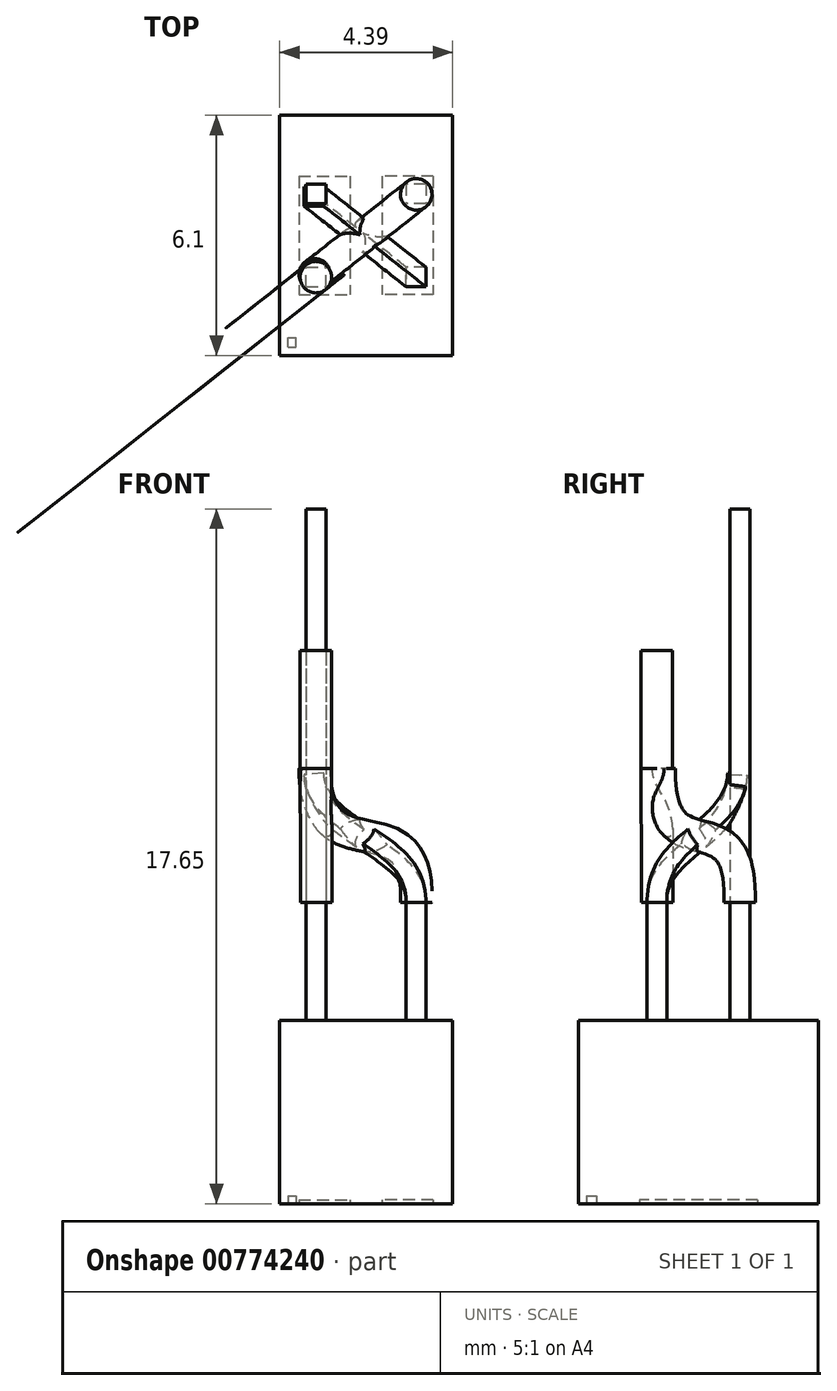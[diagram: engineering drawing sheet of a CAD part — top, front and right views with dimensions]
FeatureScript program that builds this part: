
annotation { "Feature Type Name" : "Feature", "Feature Type Description" : "" }
export const myFeature = defineFeature(function(context is Context, id is Id, definition is map)
    precondition{}
    {
        {
            var Q0;
            Q0=qCreatedBy(makeId("Top.planeOp"),FACE);
            var sketch = newSketch(context, id + "F0", { "sketchPlane" : qUnion([Q0])});
            skLineSegment(sketch, "E0.bottom", {"start": v(-4.39, 6.1) * mm, "end": v(0, 6.1) * mm});
            skLineSegment(sketch, "E0.top", {"start": v(-4.39, 0) * mm, "end": v(0, 0) * mm});
            skLineSegment(sketch, "E0.left", {"start": v(-4.39, 6.1) * mm, "end": v(-4.39, 0) * mm});
            skLineSegment(sketch, "E0.right", {"start": v(0, 6.1) * mm, "end": v(0, 0) * mm});
            skLineSegment(sketch, "E1", {"start": v(-2.2, -2.66) * mm, "end": v(-2.2, -2.66) * mm});
            skPoint(sketch, "E1.startSnap0", {"position": v(-2.2, 6.1) * mm});
            skPoint(sketch, "E1.endSnap0", {"position": v(-2.2, 0) * mm});
            skLineSegment(sketch, "E2", {"start": v(-4.39, 3.05) * mm, "end": v(0, 3.05) * mm, "construction": true});
            skLineSegment(sketch, "E3.bottom", {"start": v(-3.9, 4.55) * mm, "end": v(-2.6, 4.55) * mm});
            skLineSegment(sketch, "E3.top", {"start": v(-3.9, 1.55) * mm, "end": v(-2.6, 1.55) * mm});
            skLineSegment(sketch, "E3.left", {"start": v(-3.9, 4.55) * mm, "end": v(-3.9, 1.55) * mm});
            skLineSegment(sketch, "E3.right", {"start": v(-2.6, 4.55) * mm, "end": v(-2.6, 1.55) * mm});
            skLineSegment(sketch, "E4", {"start": v(-3.9, 3.05) * mm, "end": v(-2.6, 3.05) * mm, "construction": true});
            skLineSegment(sketch, "E5", {"start": v(-3.25, 4.55) * mm, "end": v(-3.25, 1.55) * mm, "construction": true});
            skLineSegment(sketch, "E6", {"start": v(-2.2, 6.61) * mm, "end": v(-2.2, -0.8) * mm, "construction": true});
            skLineSegment(sketch, "E7.MirrorCS", {"start": v(-1.79, 4.55) * mm, "end": v(-1.79, 1.55) * mm});
            skLineSegment(sketch, "E8.MirrorCS", {"start": v(-0.49, 4.55) * mm, "end": v(-1.79, 4.55) * mm});
            skLineSegment(sketch, "E9.MirrorCS", {"start": v(-0.49, 4.55) * mm, "end": v(-0.49, 1.55) * mm});
            skLineSegment(sketch, "E10.MirrorCS", {"start": v(-0.49, 1.55) * mm, "end": v(-1.79, 1.55) * mm});
            skLineSegment(sketch, "E11.bottom", {"start": v(-4.17, 0.2) * mm, "end": v(-3.97, 0.2) * mm});
            skLineSegment(sketch, "E11.top", {"start": v(-4.17, 0.46) * mm, "end": v(-3.97, 0.46) * mm});
            skLineSegment(sketch, "E11.left", {"start": v(-4.17, 0.2) * mm, "end": v(-4.17, 0.46) * mm});
            skLineSegment(sketch, "E11.right", {"start": v(-3.97, 0.2) * mm, "end": v(-3.97, 0.46) * mm});
            skSolve(sketch);
        }
        {
            var Q0;
            Q0=makeQuery(id+"F0.imprint","IMPRINT",FACE,{"disambiguationData":[TD([[makeQuery(id+"F0.imprint","IMPRINT",EDGE,{"derivedFrom":sQuery(id+"F0.wireOp",EDGE,"E0.bottom")}),-1.0]])]});
            var Q1;
            Q1=makeQuery(id+"F0.imprint","IMPRINT",FACE,{"disambiguationData":[TD([[makeQuery(id+"F0.imprint","IMPRINT",EDGE,{"derivedFrom":sQuery(id+"F0.wireOp",EDGE,"E3.bottom")}),-1.0]])]});
            var Q2;
            Q2=makeQuery(id+"F0.imprint","IMPRINT",FACE,{"disambiguationData":[TD([[makeQuery(id+"F0.imprint","IMPRINT",EDGE,{"derivedFrom":sQuery(id+"F0.wireOp",EDGE,"E7.MirrorCS")}),1.0]])]});
            var Q3;
            Q3=makeQuery(id+"F0.imprint","IMPRINT",FACE,{"disambiguationData":[TD([[makeQuery(id+"F0.imprint","IMPRINT",EDGE,{"derivedFrom":sQuery(id+"F0.wireOp",EDGE,"E11.bottom")}),1.0]])]});
            extrude(context, id + "F1", {"entities" : qUnion([Q0, Q1, Q2, Q3]), "depth" : 4.65 * mm, "offsetDistance" : 25 * mm});
        }
        {
            var Q0;
            Q0=makeQuery(id+"F0.imprint","IMPRINT",FACE,{"disambiguationData":[TD([[makeQuery(id+"F0.imprint","IMPRINT",EDGE,{"derivedFrom":sQuery(id+"F0.wireOp",EDGE,"E3.bottom")}),-1.0]])]});
            var Q1;
            Q1=makeQuery(id+"F0.imprint","IMPRINT",FACE,{"disambiguationData":[TD([[makeQuery(id+"F0.imprint","IMPRINT",EDGE,{"derivedFrom":sQuery(id+"F0.wireOp",EDGE,"E7.MirrorCS")}),1.0]])]});
            extrude(context, id + "F2", {"entities" : qUnion([Q0, Q1]), "operationType" : NewBodyOperationType.REMOVE, "depth" : .1 * mm, "offsetDistance" : 25 * mm});
        }
        {
            var Q0;
            Q0=makeQuery(id+"F1.opExtrude","CAP_FACE",FACE,{"disambiguationData":[OSD([sQuery(id+"F0.wireOp",EDGE,"E0.bottom"),sQuery(id+"F0.wireOp",EDGE,"E0.top"),sQuery(id+"F0.wireOp",EDGE,"E0.left"),sQuery(id+"F0.wireOp",EDGE,"E0.right")])],"isStart":false});
            var sketch = newSketch(context, id + "F3", { "sketchPlane" : qUnion([Q0])});
            skLineSegment(sketch, "E12", {"start": v(-2.2, 6.1) * mm, "end": v(-2.2, 0) * mm, "construction": true});
            skLineSegment(sketch, "E13", {"start": v(-4.39, 3.05) * mm, "end": v(0, 3.05) * mm, "construction": true});
            skLineSegment(sketch, "E14.bottom", {"start": v(-3.71, 4.35) * mm, "end": v(-3.21, 4.35) * mm});
            skLineSegment(sketch, "E14.top", {"start": v(-3.71, 3.85) * mm, "end": v(-3.21, 3.85) * mm});
            skLineSegment(sketch, "E14.left", {"start": v(-3.71, 4.35) * mm, "end": v(-3.71, 3.85) * mm});
            skLineSegment(sketch, "E14.right", {"start": v(-3.21, 4.35) * mm, "end": v(-3.21, 3.85) * mm});
            skLineSegment(sketch, "E15.MirrorCS", {"start": v(-1.17, 4.35) * mm, "end": v(-1.17, 3.85) * mm});
            skLineSegment(sketch, "E16.MirrorCS", {"start": v(-0.67, 4.35) * mm, "end": v(-1.17, 4.35) * mm});
            skLineSegment(sketch, "E17.MirrorCS", {"start": v(-0.68, 4.35) * mm, "end": v(-0.68, 3.85) * mm});
            skLineSegment(sketch, "E18.MirrorCS", {"start": v(-0.67, 3.85) * mm, "end": v(-1.17, 3.85) * mm});
            skLineSegment(sketch, "E19.MirrorCS", {"start": v(-3.71, 2.24) * mm, "end": v(-3.21, 2.24) * mm});
            skLineSegment(sketch, "E20.MirrorCS", {"start": v(-3.71, 1.75) * mm, "end": v(-3.71, 2.24) * mm});
            skLineSegment(sketch, "E21.MirrorCS", {"start": v(-3.71, 1.74) * mm, "end": v(-3.21, 1.74) * mm});
            skLineSegment(sketch, "E22.MirrorCS", {"start": v(-3.21, 1.75) * mm, "end": v(-3.21, 2.24) * mm});
            skLineSegment(sketch, "E23.MirrorCS", {"start": v(-1.17, 1.75) * mm, "end": v(-1.17, 2.24) * mm});
            skLineSegment(sketch, "E24.MirrorCS", {"start": v(-0.67, 1.74) * mm, "end": v(-1.17, 1.74) * mm});
            skLineSegment(sketch, "E25.MirrorCS", {"start": v(-0.68, 1.75) * mm, "end": v(-0.68, 2.24) * mm});
            skLineSegment(sketch, "E26.MirrorCS", {"start": v(-0.67, 2.24) * mm, "end": v(-1.17, 2.24) * mm});
            skSolve(sketch);
        }
        {
            var Q0;
            Q0=makeQuery(id+"F3.imprint","IMPRINT",FACE,{"disambiguationData":[TD([[makeQuery(id+"F3.imprint","IMPRINT",EDGE,{"derivedFrom":sQuery(id+"F3.wireOp",EDGE,"E14.bottom")}),-1.0]])]});
            var Q1;
            Q1=makeQuery(id+"F3.imprint","IMPRINT",FACE,{"disambiguationData":[TD([[makeQuery(id+"F3.imprint","IMPRINT",EDGE,{"derivedFrom":sQuery(id+"F3.wireOp",EDGE,"E19.MirrorCS")}),-1.0]])]});
            var Q2;
            Q2=makeQuery(id+"F3.imprint","IMPRINT",FACE,{"disambiguationData":[TD([[makeQuery(id+"F3.imprint","IMPRINT",EDGE,{"derivedFrom":sQuery(id+"F3.wireOp",EDGE,"E23.MirrorCS")}),-1.0]])]});
            var Q3;
            Q3=makeQuery(id+"F3.imprint","IMPRINT",FACE,{"disambiguationData":[TD([[makeQuery(id+"F3.imprint","IMPRINT",EDGE,{"derivedFrom":sQuery(id+"F3.wireOp",EDGE,"E15.MirrorCS")}),1.0]])]});
            extrude(context, id + "F4", {"entities" : qUnion([Q0, Q1, Q2, Q3]), "operationType" : NewBodyOperationType.ADD, "depth" : 3 * mm, "offsetDistance" : 25 * mm});
        }
        {
            var Q0;
            Q0=makeQuery(id+"F0.imprint","IMPRINT",FACE,{"disambiguationData":[TD([[makeQuery(id+"F0.imprint","IMPRINT",EDGE,{"derivedFrom":sQuery(id+"F0.wireOp",EDGE,"E11.bottom")}),1.0]])]});
            extrude(context, id + "F5", {"entities" : qUnion([Q0]), "operationType" : NewBodyOperationType.REMOVE, "depth" : .2 * mm, "offsetDistance" : 25 * mm});
        }
        {
            var Q0;
            Q0=makeQuery(id+"F4.opExtrude","CAP_VERTEX",VERTEX,{"disambiguationData":[OSD([sQuery(id+"F3.wireOp",EDGE,"E23.MirrorCS"),sQuery(id+"F3.wireOp",EDGE,"E26.MirrorCS")])],"isStart":false});
            var Q1;
            Q1=makeQuery(id+"F4.opExtrude","CAP_VERTEX",VERTEX,{"disambiguationData":[OSD([sQuery(id+"F3.wireOp",EDGE,"E14.top"),sQuery(id+"F3.wireOp",EDGE,"E14.right")])],"isStart":false});
            var Q2;
            Q2=makeQuery(id+"F4.opExtrude","CAP_VERTEX",VERTEX,{"disambiguationData":[OSD([sQuery(id+"F3.wireOp",EDGE,"E14.top"),sQuery(id+"F3.wireOp",EDGE,"E14.right")])],"isStart":true});
            cPlane(context, id + "F6", {"entities" : qUnion([Q0, Q1, Q2]), "cplaneType" : CPlaneType.THREE_POINT, "offset" : 25 * mm, "width" : 150 * mm, "height" : 150 * mm});
        }
        {
            var Q0;
            Q0=qCreatedBy(id+"F6.planeOp",FACE);
            var sketch = newSketch(context, id + "F7", { "sketchPlane" : qUnion([Q0])});
            skFitSpline(sketch, "E27", {"points": [v(1.95, 7.66) * mm, v(5.26, 10.93) * mm], "startDerivative": vector(-0.1, 4.67) * mm, "endDerivative": vector(0.28, 4.83) * mm});
            skSolve(sketch);
        }
        {
            var Q0;
            Q0=makeQuery(id+"F4.opExtrude","CAP_FACE",FACE,{"disambiguationData":[OSD([sQuery(id+"F3.wireOp",EDGE,"E23.MirrorCS"),sQuery(id+"F3.wireOp",EDGE,"E24.MirrorCS"),sQuery(id+"F3.wireOp",EDGE,"E25.MirrorCS"),sQuery(id+"F3.wireOp",EDGE,"E26.MirrorCS")])],"isStart":false});
            var Q1;
            Q1=sQuery(id+"F7.wireOp",EDGE,"E27");
            sweep(context, id + "F8", {"operationType" : NewBodyOperationType.ADD, "profiles" : qUnion([Q0]), "path" : qUnion([Q1])});
        }
        {
            var Q0;
            Q0=makeQuery(id+"F4.opExtrude","CAP_FACE",FACE,{"disambiguationData":[OSD([sQuery(id+"F3.wireOp",EDGE,"E14.bottom"),sQuery(id+"F3.wireOp",EDGE,"E14.top"),sQuery(id+"F3.wireOp",EDGE,"E14.left"),sQuery(id+"F3.wireOp",EDGE,"E14.right")])],"isStart":false});
            extrude(context, id + "F9", {"entities" : qUnion([Q0]), "operationType" : NewBodyOperationType.ADD, "depth" : 10 * mm, "offsetDistance" : 25 * mm});
        }
        {
            var Q0;
            Q0=makeQuery(id+"F4.opExtrude","CAP_VERTEX",VERTEX,{"disambiguationData":[OSD([sQuery(id+"F3.wireOp",EDGE,"E19.MirrorCS"),sQuery(id+"F3.wireOp",EDGE,"E22.MirrorCS")])],"isStart":false});
            var Q1;
            Q1=makeQuery(id+"F4.opExtrude","CAP_VERTEX",VERTEX,{"disambiguationData":[OSD([sQuery(id+"F3.wireOp",EDGE,"E19.MirrorCS"),sQuery(id+"F3.wireOp",EDGE,"E22.MirrorCS")])],"isStart":true});
            var Q2;
            Q2=makeQuery(id+"F4.opExtrude","CAP_VERTEX",VERTEX,{"disambiguationData":[OSD([sQuery(id+"F3.wireOp",EDGE,"E15.MirrorCS"),sQuery(id+"F3.wireOp",EDGE,"E18.MirrorCS")])],"isStart":true});
            cPlane(context, id + "F10", {"entities" : qUnion([Q0, Q1, Q2]), "cplaneType" : CPlaneType.THREE_POINT, "offset" : 25 * mm, "width" : 150 * mm, "height" : 150 * mm});
        }
        {
            var Q0;
            Q0=qCreatedBy(id+"F10.planeOp",FACE);
            var sketch = newSketch(context, id + "F11", { "sketchPlane" : qUnion([Q0])});
            skFitSpline(sketch, "E28", {"points": [v(1.46, 7.7) * mm, v(1.47, 11.1) * mm], "startDerivative": vector(0, 3.4) * mm, "endDerivative": vector(0, 3.4) * mm});
            skFitSpline(sketch, "E29", {"points": [v(-1.81, 7.7) * mm, v(1.47, 11.1) * mm], "startDerivative": vector(-0.28, 8.28) * mm, "endDerivative": vector(-0.14, 8.84) * mm});
            skSolve(sketch);
        }
        {
            var Q0;
            Q0=makeQuery(id+"F4.opExtrude","CAP_FACE",FACE,{"disambiguationData":[OSD([sQuery(id+"F3.wireOp",EDGE,"E19.MirrorCS"),sQuery(id+"F3.wireOp",EDGE,"E20.MirrorCS"),sQuery(id+"F3.wireOp",EDGE,"E21.MirrorCS"),sQuery(id+"F3.wireOp",EDGE,"E22.MirrorCS")])],"isStart":false});
            var sketch = newSketch(context, id + "F12", { "sketchPlane" : qUnion([Q0])});
            skCircle(sketch, "E30", {"center": v(-3.46, 2) * mm, "radius": 0.4 * mm});
            skCircle(sketch, "E31", {"center": v(-0.92, 4.1) * mm, "radius": 0.4 * mm});
            skSolve(sketch);
        }
        {
            var Q0;
            Q0=makeQuery(id+"F12.imprint","IMPRINT",FACE,{"disambiguationData":[TD([[makeQuery(id+"F12.imprint","IMPRINT",EDGE,{"derivedFrom":sQuery(id+"F12.wireOp",EDGE,"E30")}),1.0]])]});
            var Q1;
            Q1=makeQuery(id+"F12.imprint","IMPRINT",FACE,{"disambiguationData":[TD([[makeQuery(id+"F12.imprint","IMPRINT",EDGE,{"derivedFrom":makeQuery(id+"F4.opExtrude","CAP_EDGE",EDGE,{"disambiguationData":[OSD([sQuery(id+"F3.wireOp",EDGE,"E19.MirrorCS")])],"isStart":false})}),-1.0]])]});
            var Q2;
            Q2=sQuery(id+"F11.wireOp",EDGE,"E28");
            sweep(context, id + "F13", {"profiles" : qUnion([Q0, Q1]), "path" : qUnion([Q2])});
        }
        {
            var Q0;
            Q0=makeQuery(id+"F12.imprint","IMPRINT",FACE,{"disambiguationData":[TD([[makeQuery(id+"F12.imprint","IMPRINT",EDGE,{"derivedFrom":sQuery(id+"F12.wireOp",EDGE,"E31")}),1.0]])]});
            var Q1;
            Q1=sQuery(id+"F11.wireOp",EDGE,"E29");
            sweep(context, id + "F14", {"operationType" : NewBodyOperationType.ADD, "profiles" : qUnion([Q0]), "path" : qUnion([Q1])});
        }
        {
            var Q0;
            Q0=makeQuery(id+"F13.opSweep","CAP_FACE",FACE,{"disambiguationData":[OSD([sQuery(id+"F11.wireOp",VERTEX,"E28.end"),sQuery(id+"F12.wireOp",EDGE,"E30")])],"isStart":false});
            extrude(context, id + "F15", {"entities" : qUnion([Q0]), "operationType" : NewBodyOperationType.ADD, "depth" : 3 * mm, "offsetDistance" : 25 * mm});
        }
    });
